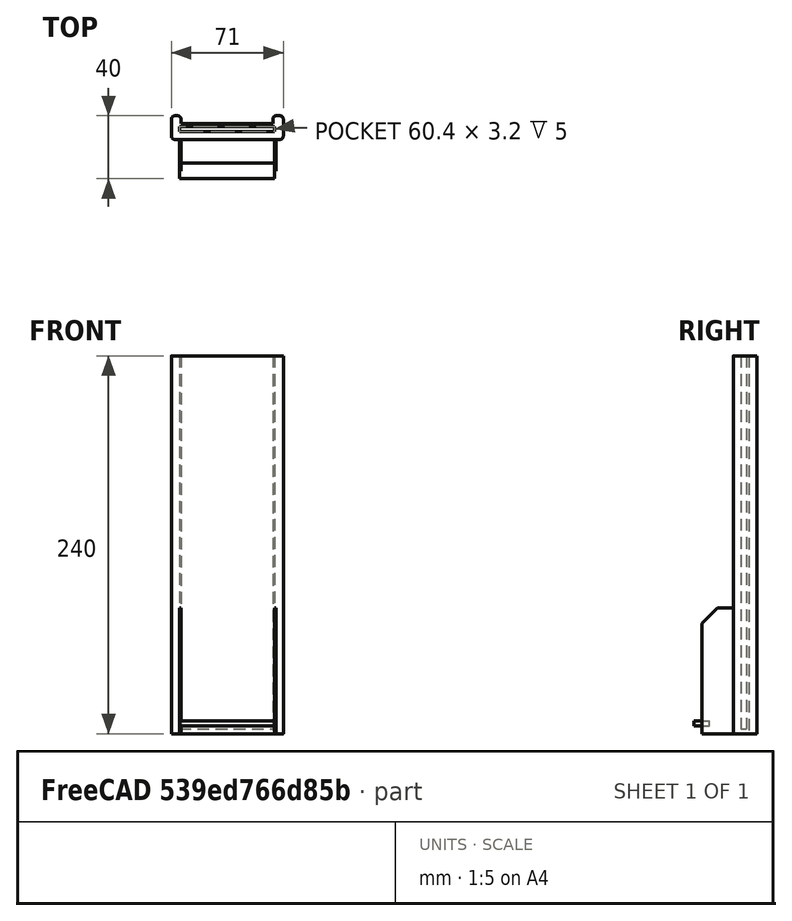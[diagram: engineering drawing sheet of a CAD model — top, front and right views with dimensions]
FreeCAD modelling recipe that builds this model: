
FCSTD DOCUMENT  (FreeCAD 0.19R24291 (Git))
Label: magnetic-slide
License: All rights reserved
LicenseURL: http://en.wikipedia.org/wiki/All_rights_reserved
objects: Part::Box×8, Part::MultiFuse×3, Part::Cut×2, Part::Fillet×1, Part::Chamfer×1
note: 15 computed .brp shape members not serialized (recipe doc carries the construction recipe); baked Part::Feature solids carry a one-line shape summary decoded from their .brp

FEATURE [Part::Box] Box  label="Single-Magnet"
  AttacherType = Attacher::AttachEngine3D
  Height = 3.2
  Length = 60.4
  Width = 10
FEATURE [Part::Box] Box001  label="25-Single-Magnets"
  AttacherType = Attacher::AttachEngine3D
  Height = 3.2
  Length = 60.4
  Placement = pos=(0,-5,0) rot=(0,0,1;0rad)
  Width = 250
FEATURE [Part::Box] Box002  label="To-Cut-From"
  AttacherType = Attacher::AttachEngine3D
  Height = 15
  Length = 71
  Placement = pos=(-5,-5,-5) rot=(0,0,1;0rad)
  Width = 240
FEATURE [Part::Box] Box003  label="25-Single-Magnets001"
  AttacherType = Attacher::AttachEngine3D
  Height = 3.2
  Length = 60.4
  Width = 250
FEATURE [Part::MultiFuse] Fusion  label="Magnet-Cutout"
  Placement = pos=(0,-18,0) rot=(0,0,1;0rad)
  Shapes = -> [Box001,Box003]
FEATURE [Part::Box] Box004  label="25-Single-Magnets002"
  AttacherType = Attacher::AttachEngine3D
  Height = 13.2
  Length = 58.4
  Placement = pos=(1,7,0) rot=(0,0,1;0rad)
  Width = 250
FEATURE [Part::Box] Box005  label="25-Single-Magnets003"
  AttacherType = Attacher::AttachEngine3D
  Height = 13.2
  Length = 58.4
  Placement = pos=(1,-9,0) rot=(0,0,1;0rad)
  Width = 250
FEATURE [Part::MultiFuse] Fusion001  label="Slide-Cutout"
  Placement = pos=(0,0,5) rot=(0,0,1;0rad)
  Shapes = -> [Box005,Box004]
FEATURE [Part::Cut] Cut
  Base = -> Box002
  Tool = -> Fusion001
FEATURE [Part::Cut] Cut001  label="Slide-V1"
  Base = -> Cut
  Placement = pos=(0,30,230) rot=(1,0,0;4.71239rad)
  Tool = -> Fusion
FEATURE [Part::Box] Box006  label="Support"
  AttacherType = Attacher::AttachEngine3D
  Height = 80
  Length = 1
  Placement = pos=(0,5,-5) rot=(0,0,1;0rad)
  Width = 20
FEATURE [Part::Box] Box007  label="Support001"
  AttacherType = Attacher::AttachEngine3D
  Height = 80
  Length = 1
  Placement = pos=(60.5,5,-5) rot=(0,0,1;0rad)
  Width = 20
FEATURE [Part::MultiFuse] Fusion002
  Shapes = -> [Box007,Cut001,Box006]
FEATURE [Part::Fillet] Fillet
  Base = -> Fusion002
  Edges = 8 edges r=2: [Edge2,Edge4,Edge17,Edge18,Edge35,Edge36,Edge37,Edge38]
FEATURE [Part::Chamfer] Chamfer
  Base = -> Fillet
  Edges = 2 edges r=10: [Edge85,Edge91]
